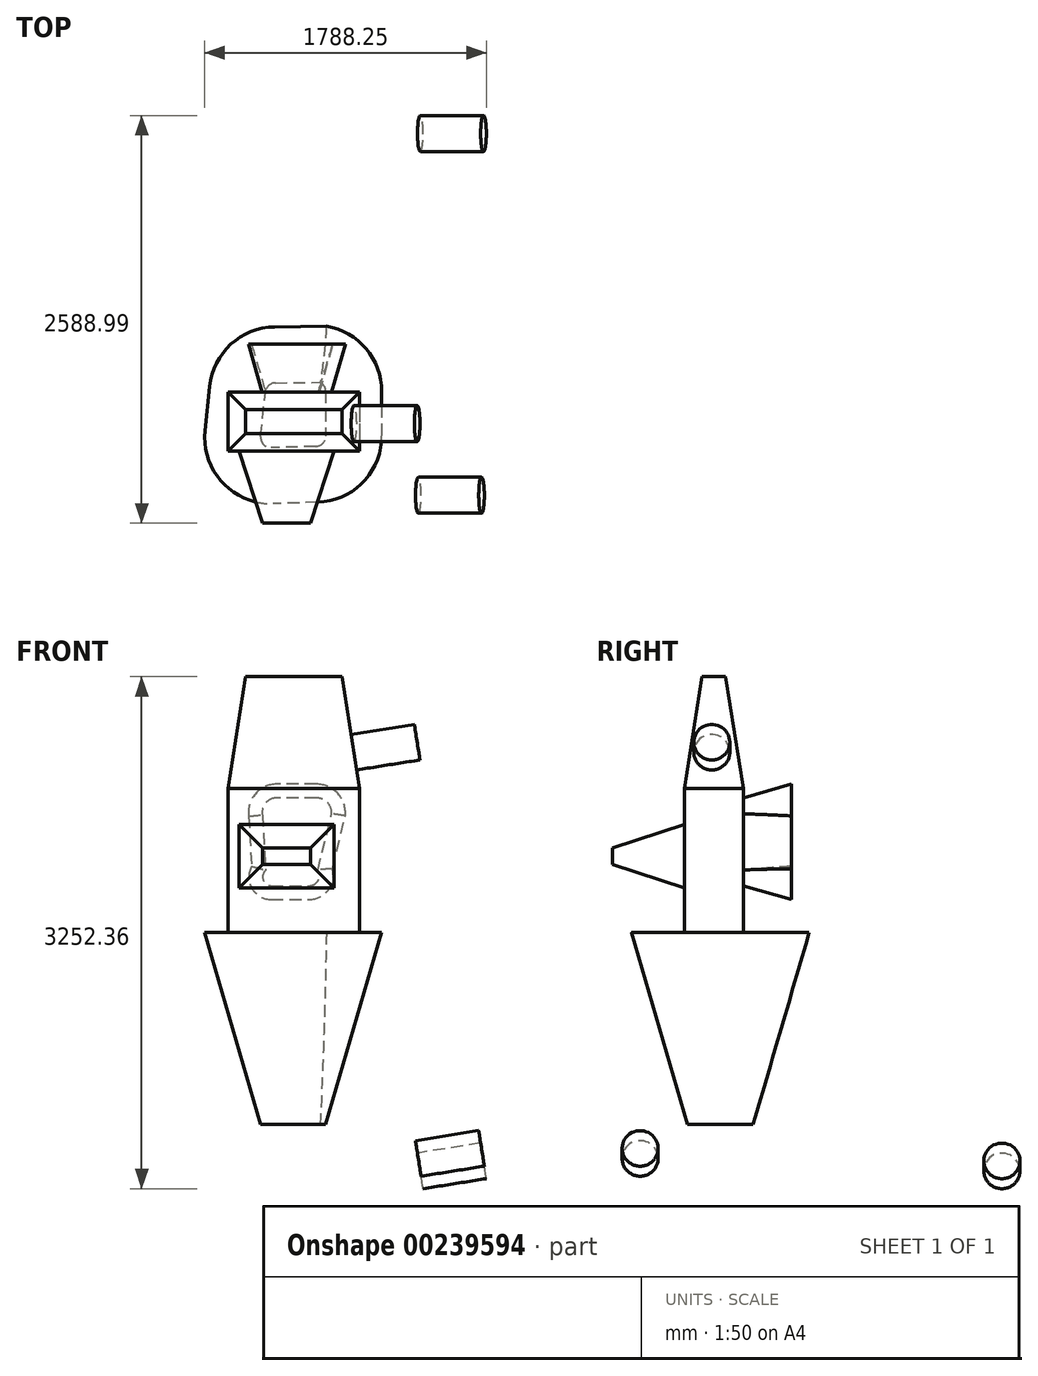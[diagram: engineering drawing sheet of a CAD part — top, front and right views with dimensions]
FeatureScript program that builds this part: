
annotation { "Feature Type Name" : "Feature", "Feature Type Description" : "" }
export const myFeature = defineFeature(function(context is Context, id is Id, definition is map)
    precondition{}
    {
        {
            var Q0;
            Q0=qCreatedBy(makeId("Top.planeOp"),FACE);
            var sketch = newSketch(context, id + "F0", { "sketchPlane" : qUnion([Q0])});
            skLineSegment(sketch, "E0", {"start": v(-43.69, 58.35) * mm, "end": v(239.66, 62.3) * mm});
            skArc(sketch, "E1", {"start": v(276.59, 3.7) * mm, "mid": v(266.59, 38.34) * mm, "end": v(239.66, 62.3) * mm});
            skLineSegment(sketch, "E2", {"start": v(276.59, 3.7) * mm, "end": v(276.59, -279.68) * mm});
            skArc(sketch, "E3", {"start": v(213.64, -344.62) * mm, "mid": v(258.27, -324.9) * mm, "end": v(276.59, -279.68) * mm});
            skLineSegment(sketch, "E4", {"start": v(213.64, -344.62) * mm, "end": v(-69.6, -353.47) * mm});
            skArc(sketch, "E5", {"start": v(-136.27, -281.9) * mm, "mid": v(-119.17, -332.81) * mm, "end": v(-69.6, -353.47) * mm});
            skArc(sketch, "E6", {"start": v(-43.69, 58.35) * mm, "mid": v(-86.66, 41.3) * mm, "end": v(-107.42, 0) * mm});
            skLineSegment(sketch, "E7", {"start": v(-107.42, 0) * mm, "end": v(-136.27, -281.9) * mm});
            skSolve(sketch);
        }
        {
            var Q0;
            Q0 = qSketchRegion(id + "F0", true);
            extrude(context, id + "F1", {"entities" : qUnion([Q0]), "depth" : 1219.2 * mm, "hasDraft" : true, "draftAngle" : 16.25 * degree});
        }
        {
            var Q0;
            Q0=makeQuery(id+"F1.opExtrude","CAP_FACE",FACE,{"disambiguationData":[OSD([sQuery(id+"F0.wireOp",EDGE,"E0"),sQuery(id+"F0.wireOp",EDGE,"E1"),sQuery(id+"F0.wireOp",EDGE,"E2"),sQuery(id+"F0.wireOp",EDGE,"E3"),sQuery(id+"F0.wireOp",EDGE,"E4"),sQuery(id+"F0.wireOp",EDGE,"E5"),sQuery(id+"F0.wireOp",EDGE,"E6"),sQuery(id+"F0.wireOp",EDGE,"E7")])],"isStart":false});
            var sketch = newSketch(context, id + "F2", { "sketchPlane" : qUnion([Q0])});
            skLineSegment(sketch, "E8.bottom", {"start": v(492.4, 0) * mm, "end": v(-345.5, 0) * mm});
            skLineSegment(sketch, "E8.top", {"start": v(492.4, -375.2) * mm, "end": v(-345.5, -375.2) * mm});
            skLineSegment(sketch, "E8.left", {"start": v(492.4, 0) * mm, "end": v(492.4, -375.2) * mm});
            skLineSegment(sketch, "E8.right", {"start": v(-345.5, 0) * mm, "end": v(-345.5, -375.2) * mm});
            skPoint(sketch, "E8.middle", {"position": v(73.45, -187.6) * mm});
            skSolve(sketch);
        }
        {
            var Q0;
            Q0 = qSketchRegion(id + "F2", true);
            extrude(context, id + "F3", {"entities" : qUnion([Q0]), "operationType" : NewBodyOperationType.ADD, "depth" : 914.4 * mm});
        }
        {
            var Q0;
            Q0=makeQuery(id+"F3.opExtrude","SWEPT_FACE",FACE,{"disambiguationData":[OSD([sQuery(id+"F2.wireOp",EDGE,"E8.bottom")])]});
            var sketch = newSketch(context, id + "F4", { "sketchPlane" : qUnion([Q0])});
            skLineSegment(sketch, "E9", {"start": v(68.47, 1516.6) * mm, "end": v(-172.03, 1516.6) * mm});
            skLineSegment(sketch, "E10", {"start": v(105.55, 1613.72) * mm, "end": v(126.04, 1967.1) * mm});
            skLineSegment(sketch, "E11", {"start": v(-226.92, 1616.55) * mm, "end": v(-314.04, 1974.12) * mm});
            skLineSegment(sketch, "E12", {"start": v(35.63, 2074.36) * mm, "end": v(-218.05, 2074.36) * mm});
            skArc(sketch, "E13", {"start": v(68.47, 1516.6) * mm, "mid": v(120.45, 1552.4) * mm, "end": v(105.55, 1613.72) * mm});
            skArc(sketch, "E14", {"start": v(-226.92, 1616.55) * mm, "mid": v(-229.04, 1550.33) * mm, "end": v(-172.03, 1516.6) * mm});
            skArc(sketch, "E15", {"start": v(-218.05, 2074.36) * mm, "mid": v(-287.44, 2044.73) * mm, "end": v(-314.04, 1974.12) * mm});
            skArc(sketch, "E16", {"start": v(126.04, 1967.1) * mm, "mid": v(105.77, 2041.75) * mm, "end": v(35.63, 2074.36) * mm});
            skSolve(sketch);
        }
        {
            var Q0;
            Q0 = qSketchRegion(id + "F4", true);
            extrude(context, id + "F5", {"entities" : qUnion([Q0]), "operationType" : NewBodyOperationType.ADD, "depth" : 304.8 * mm, "hasDraft" : true, "draftAngle" : 16 * degree});
        }
        {
            var Q0;
            Q0=makeQuery(id+"F3.opExtrude","SWEPT_FACE",FACE,{"disambiguationData":[OSD([sQuery(id+"F2.wireOp",EDGE,"E8.top")])]});
            var sketch = newSketch(context, id + "F6", { "sketchPlane" : qUnion([Q0])});
            skLineSegment(sketch, "E17.bottom", {"start": v(329.46, 1502.68) * mm, "end": v(-274.4, 1502.68) * mm});
            skLineSegment(sketch, "E17.top", {"start": v(329.46, 1904.72) * mm, "end": v(-274.4, 1904.72) * mm});
            skLineSegment(sketch, "E17.left", {"start": v(329.46, 1502.68) * mm, "end": v(329.46, 1904.72) * mm});
            skLineSegment(sketch, "E17.right", {"start": v(-274.4, 1502.68) * mm, "end": v(-274.4, 1904.72) * mm});
            skPoint(sketch, "E17.middle", {"position": v(27.53, 1703.7) * mm});
            skSolve(sketch);
        }
        {
            var Q0;
            Q0=makeQuery(id+"F6.imprint","IMPRINT",FACE,{"disambiguationData":[TD([[makeQuery(id+"F6.imprint","IMPRINT",EDGE,{"derivedFrom":sQuery(id+"F6.wireOp",EDGE,"E17.bottom")}),-1.0]])]});
            extrude(context, id + "F7", {"entities" : qUnion([Q0]), "operationType" : NewBodyOperationType.ADD, "depth" : 457.2 * mm, "hasDraft" : true, "draftAngle" : 18 * degree, "draftPullDirection" : true});
        }
        {
            var Q0;
            Q0=makeQuery(id+"F3.opExtrude","SWEPT_FACE",FACE,{"disambiguationData":[OSD([sQuery(id+"F2.wireOp",EDGE,"E8.right")])]});
            var sketch = newSketch(context, id + "F8", { "sketchPlane" : qUnion([Q0])});
            skCircle(sketch, "E18", {"center": v(187.43, 1708.45) * mm, "radius": 164.23 * mm});
            skCircle(sketch, "E19", {"center": v(306.7, 1821.34) * mm, "radius": 1926.32 * mm});
            skSolve(sketch);
        }
        {
            var Q0;
            Q0=sQuery(id+"F8.wireOp",EDGE,"E18");
            extrude(context, id + "F9", {"bodyType" : ToolBodyType.SURFACE, "surfaceEntities" : qUnion([Q0]), "depth" : 609.6 * mm});
        }
        {
            var Q0;
            Q0=makeQuery(id+"F3.opExtrude","CAP_FACE",FACE,{"disambiguationData":[OSD([sQuery(id+"F2.wireOp",EDGE,"E8.bottom"),sQuery(id+"F2.wireOp",EDGE,"E8.top"),sQuery(id+"F2.wireOp",EDGE,"E8.left"),sQuery(id+"F2.wireOp",EDGE,"E8.right")])],"isStart":false});
            extrude(context, id + "F10", {"entities" : qUnion([Q0]), "operationType" : NewBodyOperationType.ADD, "depth" : 711.2 * mm, "hasDraft" : true, "draftAngle" : 9 * degree, "draftPullDirection" : true});
        }
        {
            var Q0;
            Q0=makeQuery(id+"F10.opExtrude","SWEPT_FACE",FACE,{"disambiguationData":[OSD([sQuery(id+"F2.wireOp",EDGE,"E8.left")])]});
            var sketch = newSketch(context, id + "F11", { "sketchPlane" : qUnion([Q0])});
            skCircle(sketch, "E20", {"center": v(-200.35, 2264.56) * mm, "radius": 114.3 * mm});
            skCircle(sketch, "E21", {"center": v(1642.3, -428.23) * mm, "radius": 114.3 * mm});
            skCircle(sketch, "E22", {"center": v(-655.64, -347.89) * mm, "radius": 114.3 * mm});
            skSolve(sketch);
        }
        {
            var Q0;
            Q0 = qSketchRegion(id + "F11", true);
            extrude(context, id + "F12", {"entities" : qUnion([Q0]), "depth" : 406.4 * mm});
        }
    });
